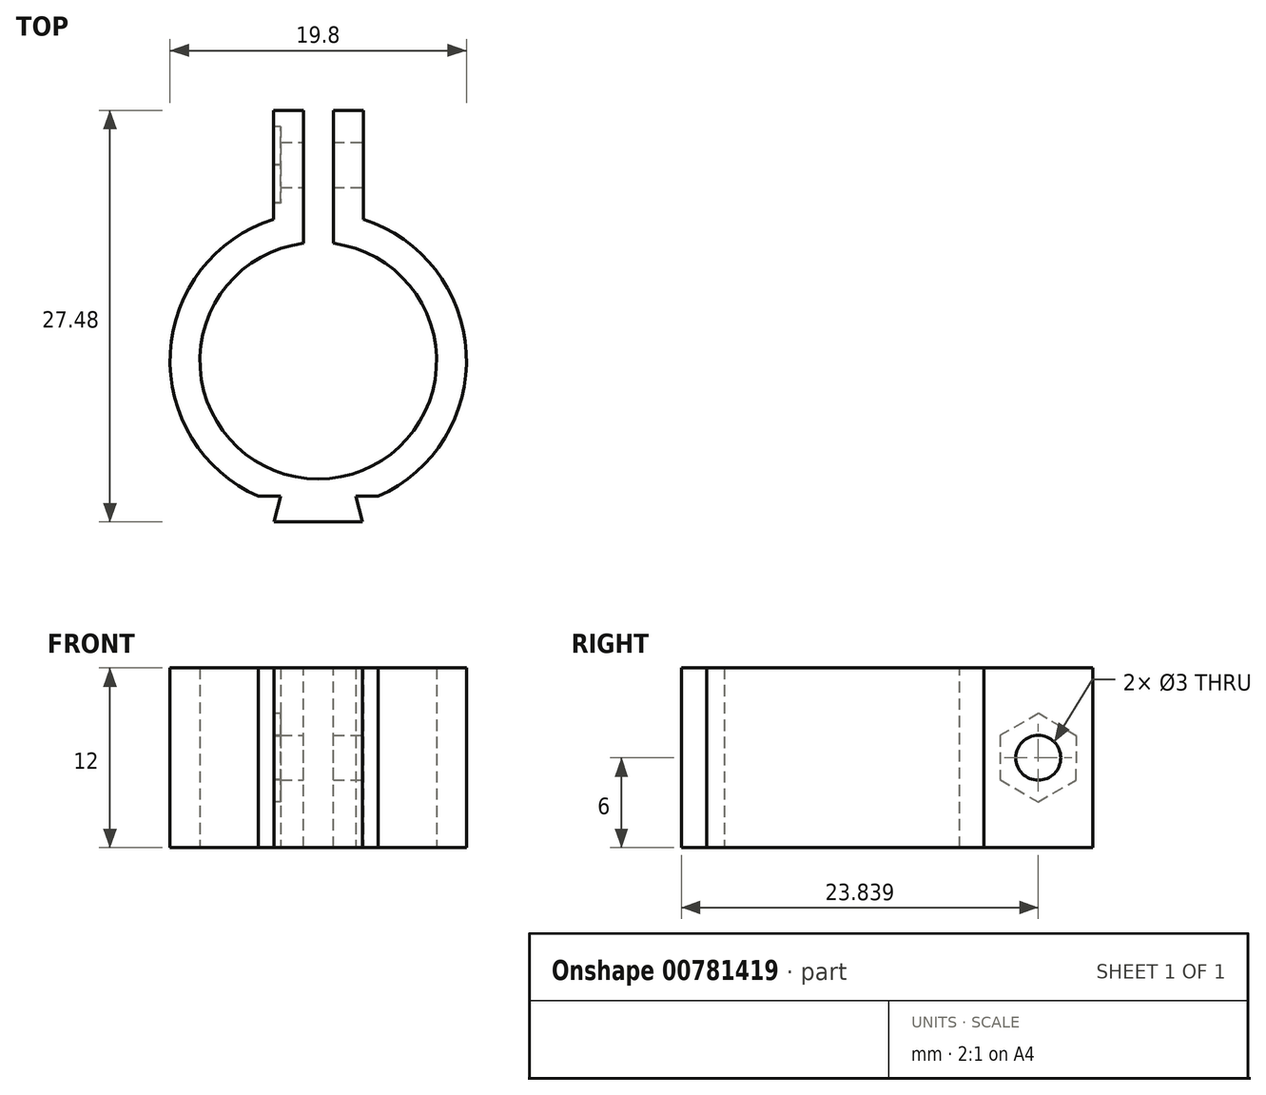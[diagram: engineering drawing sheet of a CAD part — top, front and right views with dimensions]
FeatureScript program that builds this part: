
annotation { "Feature Type Name" : "Feature", "Feature Type Description" : "" }
export const myFeature = defineFeature(function(context is Context, id is Id, definition is map)
    precondition{}
    {
        {
            var Q0;
            Q0=qCreatedBy(makeId("Top.planeOp"),FACE);
            var sketch = newSketch(context, id + "F0", { "sketchPlane" : qUnion([Q0])});
            skCircle(sketch, "E0", {"center": v(0, 0) * mm, "radius": 7.9 * mm});
            skCircle(sketch, "E1", {"center": v(0, 0) * mm, "radius": 9.9 * mm});
            skCircle(sketch, "E2", {"center": v(0, 0) * mm, "radius": 8.85 * mm, "construction": true});
            skLineSegment(sketch, "E3", {"start": v(0, -8.85) * mm, "end": v(-2.8, -8.85) * mm, "construction": true});
            skSolve(sketch);
        }
        {
            var Q0;
            Q0 = qSketchRegion(id + "F0", true);
            extrude(context, id + "F1", {"entities" : qUnion([Q0]), "depth" : 12 * mm, "offsetDistance" : 25 * mm});
        }
        {
            var Q0;
            Q0=qCreatedBy(makeId("Top.planeOp"),FACE);
            var sketch = newSketch(context, id + "F2", { "sketchPlane" : qUnion([Q0])});
            skLineSegment(sketch, "E4", {"start": v(0, -9.06) * mm, "end": v(4, -9.06) * mm});
            skLineSegment(sketch, "E5", {"start": v(0, -9.06) * mm, "end": v(-4, -9.06) * mm});
            skLineSegment(sketch, "E6", {"start": v(4, -9.06) * mm, "end": v(4, -10.76) * mm});
            skLineSegment(sketch, "E7", {"start": v(-4, -9.06) * mm, "end": v(-4, -10.76) * mm});
            skLineSegment(sketch, "E8", {"start": v(-4, -10.76) * mm, "end": v(4, -10.76) * mm});
            skSolve(sketch);
        }
        {
            var Q0;
            Q0 = qSketchRegion(id + "F2", true);
            extrude(context, id + "F3", {"entities" : qUnion([Q0]), "operationType" : NewBodyOperationType.ADD, "depth" : 12 * mm, "offsetDistance" : 25 * mm});
        }
        {
            var Q0;
            Q0=qCreatedBy(makeId("Top.planeOp"),FACE);
            var sketch = newSketch(context, id + "F4", { "sketchPlane" : qUnion([Q0])});
            skLineSegment(sketch, "E9", {"start": v(2.5, -9.06) * mm, "end": v(4, -9.06) * mm});
            skLineSegment(sketch, "E10", {"start": v(4, -9.06) * mm, "end": v(4, -10.76) * mm});
            skLineSegment(sketch, "E11.MirrorCS", {"start": v(-2.5, -9.06) * mm, "end": v(-4, -9.06) * mm});
            skLineSegment(sketch, "E12.MirrorCS", {"start": v(-4, -9.06) * mm, "end": v(-4, -10.76) * mm});
            skLineSegment(sketch, "E13", {"start": v(-2.5, -9.06) * mm, "end": v(-2.95, -10.76) * mm});
            skLineSegment(sketch, "E14", {"start": v(-2.95, -10.76) * mm, "end": v(-4, -10.76) * mm});
            skLineSegment(sketch, "E15.MirrorCS", {"start": v(2.5, -9.06) * mm, "end": v(2.95, -10.76) * mm});
            skLineSegment(sketch, "E16.MirrorCS", {"start": v(2.95, -10.76) * mm, "end": v(4, -10.76) * mm});
            skSolve(sketch);
        }
        {
            var Q0;
            Q0 = qSketchRegion(id + "F4", true);
            extrude(context, id + "F5", {"entities" : qUnion([Q0]), "operationType" : NewBodyOperationType.REMOVE, "endBound" : BoundingType.THROUGH_ALL, "depth" : 25 * mm, "offsetDistance" : 25 * mm});
        }
        {
            var Q0;
            Q0=makeQuery(id+"F3.boolean.opBoolean","MERGE",FACE,{"derivedFrom":[makeQuery(id+"F1.opExtrude","CAP_FACE",FACE,{"disambiguationData":[OSD([sQuery(id+"F0.wireOp",EDGE,"E0"),sQuery(id+"F0.wireOp",EDGE,"E1")])],"isStart":false}),makeQuery(id+"F3.opExtrude","CAP_FACE",FACE,{"disambiguationData":[OSD([sQuery(id+"F2.wireOp",EDGE,"E4"),sQuery(id+"F2.wireOp",EDGE,"E5"),sQuery(id+"F2.wireOp",EDGE,"E6"),sQuery(id+"F2.wireOp",EDGE,"E7"),sQuery(id+"F2.wireOp",EDGE,"E8")])],"isStart":false})]});
            var sketch = newSketch(context, id + "F6", { "sketchPlane" : qUnion([Q0])});
            skLineSegment(sketch, "E17.bottom", {"start": v(1, 7.84) * mm, "end": v(-1, 7.84) * mm});
            skLineSegment(sketch, "E17.top", {"start": v(1, 12.44) * mm, "end": v(-1, 12.44) * mm});
            skLineSegment(sketch, "E17.left", {"start": v(1, 7.84) * mm, "end": v(1, 12.44) * mm});
            skLineSegment(sketch, "E17.right", {"start": v(-1, 7.84) * mm, "end": v(-1, 12.44) * mm});
            skSolve(sketch);
        }
        {
            var Q0;
            Q0 = qSketchRegion(id + "F6", true);
            extrude(context, id + "F7", {"entities" : qUnion([Q0]), "operationType" : NewBodyOperationType.REMOVE, "endBound" : BoundingType.THROUGH_ALL, "oppositeDirection" : true, "depth" : 25 * mm, "offsetDistance" : 25 * mm});
        }
        {
            var Q0;
            Q0=qCreatedBy(makeId("Top.planeOp"),FACE);
            var sketch = newSketch(context, id + "F8", { "sketchPlane" : qUnion([Q0])});
            skLineSegment(sketch, "E18.bottom", {"start": v(-1, 8.72) * mm, "end": v(-3, 8.72) * mm});
            skLineSegment(sketch, "E18.top", {"start": v(-1, 16.72) * mm, "end": v(-3, 16.72) * mm});
            skLineSegment(sketch, "E18.left", {"start": v(-1, 8.72) * mm, "end": v(-1, 16.72) * mm});
            skLineSegment(sketch, "E18.right", {"start": v(-3, 8.72) * mm, "end": v(-3, 16.72) * mm});
            skLineSegment(sketch, "E19.MirrorCS", {"start": v(1, 8.72) * mm, "end": v(1, 16.72) * mm});
            skLineSegment(sketch, "E20.MirrorCS", {"start": v(1, 16.72) * mm, "end": v(3, 16.72) * mm});
            skLineSegment(sketch, "E21.MirrorCS", {"start": v(3, 8.72) * mm, "end": v(3, 16.72) * mm});
            skLineSegment(sketch, "E22.MirrorCS", {"start": v(1, 8.72) * mm, "end": v(3, 8.72) * mm});
            skSolve(sketch);
        }
        {
            var Q0;
            Q0 = qSketchRegion(id + "F8", true);
            extrude(context, id + "F9", {"entities" : qUnion([Q0]), "operationType" : NewBodyOperationType.ADD, "depth" : 12 * mm, "offsetDistance" : 25 * mm});
        }
        {
            var Q0;
            Q0=makeQuery(id+"F9.opExtrude","SWEPT_FACE",FACE,{"disambiguationData":[OSD([sQuery(id+"F8.wireOp",EDGE,"E21.MirrorCS")])]});
            var sketch = newSketch(context, id + "F10", { "sketchPlane" : qUnion([Q0])});
            skCircle(sketch, "E23", {"center": v(13.08, 6) * mm, "radius": 1.5 * mm});
            skSolve(sketch);
        }
        {
            var Q0;
            Q0 = qSketchRegion(id + "F10", true);
            extrude(context, id + "F11", {"entities" : qUnion([Q0]), "operationType" : NewBodyOperationType.REMOVE, "endBound" : BoundingType.THROUGH_ALL, "oppositeDirection" : true, "depth" : 25 * mm, "offsetDistance" : 25 * mm});
        }
        {
            var Q0;
            Q0=makeQuery(id+"F9.opExtrude","SWEPT_FACE",FACE,{"disambiguationData":[OSD([sQuery(id+"F8.wireOp",EDGE,"E18.right")])]});
            var sketch = newSketch(context, id + "F12", { "sketchPlane" : qUnion([Q0])});
            skCircle(sketch, "E24.cCircle", {"center": v(-13.08, 6) * mm, "radius": 2.55 * mm, "construction": true});
            skLineSegment(sketch, "E24.0", {"start": v(-15.64, 7.45) * mm, "end": v(-13.1, 8.94) * mm});
            skLineSegment(sketch, "E24.1", {"start": v(-13.1, 8.94) * mm, "end": v(-10.54, 7.5) * mm});
            skLineSegment(sketch, "E24.2", {"start": v(-10.54, 7.5) * mm, "end": v(-10.52, 4.55) * mm});
            skLineSegment(sketch, "E24.3", {"start": v(-10.52, 4.55) * mm, "end": v(-13.05, 3.06) * mm});
            skLineSegment(sketch, "E24.4", {"start": v(-13.05, 3.06) * mm, "end": v(-15.62, 4.5) * mm});
            skLineSegment(sketch, "E24.5", {"start": v(-15.62, 4.5) * mm, "end": v(-15.64, 7.45) * mm});
            skPoint(sketch, "E24.0.midPoint", {"position": v(-14.37, 8.2) * mm});
            skSolve(sketch);
        }
        {
            var Q0;
            Q0 = qSketchRegion(id + "F12", true);
            extrude(context, id + "F13", {"entities" : qUnion([Q0]), "operationType" : NewBodyOperationType.REMOVE, "oppositeDirection" : true, "depth" : 0.5 * mm, "offsetDistance" : 25 * mm});
        }
    });
